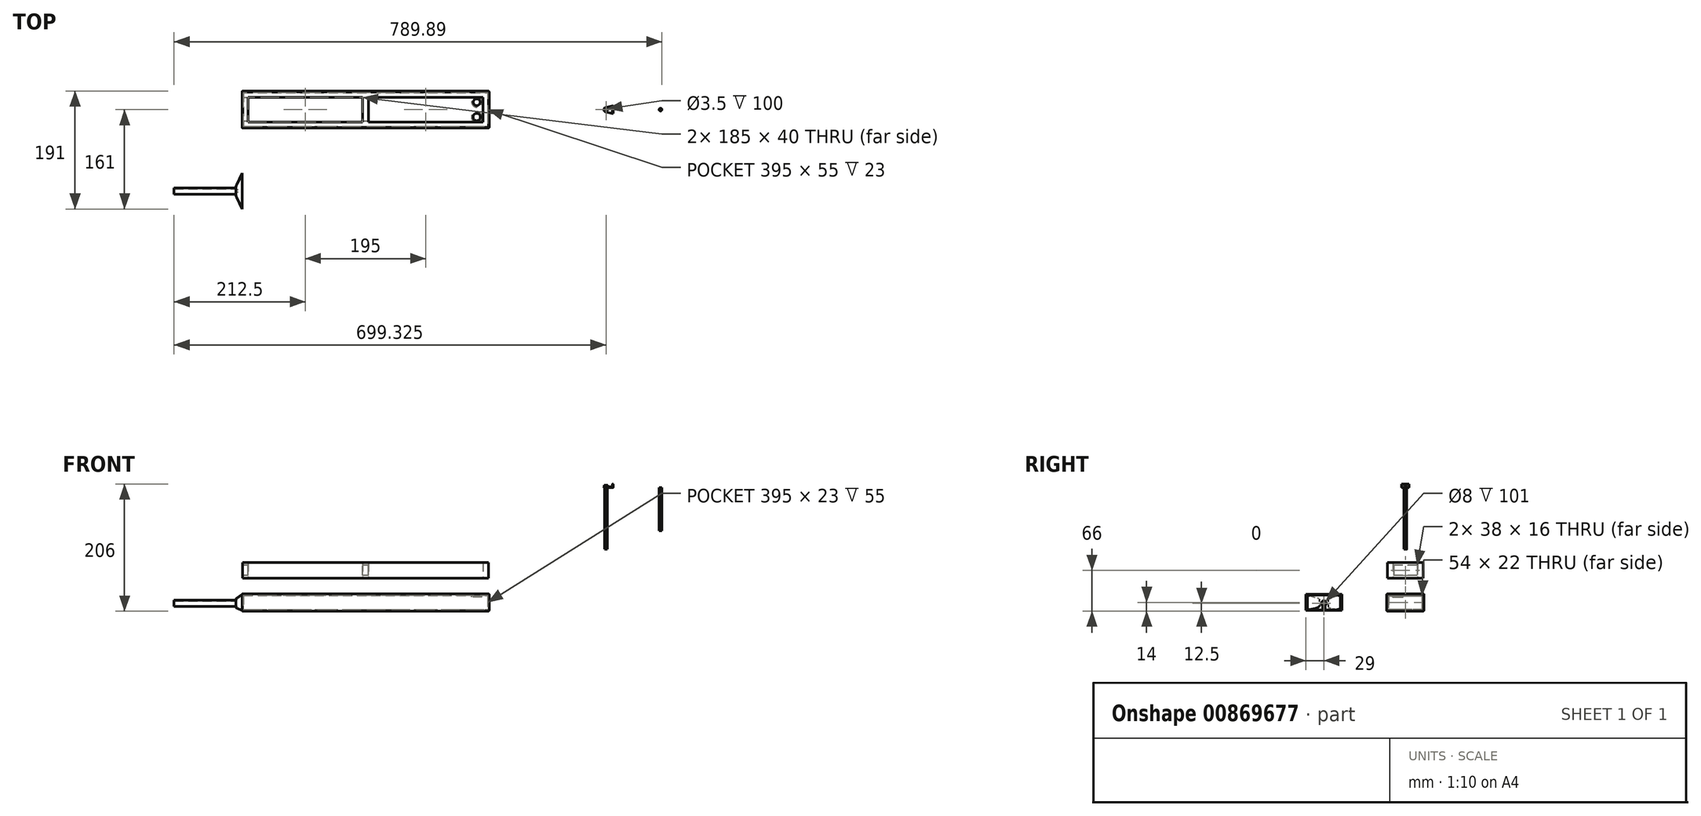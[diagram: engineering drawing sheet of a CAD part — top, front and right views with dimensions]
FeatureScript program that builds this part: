
annotation { "Feature Type Name" : "Feature", "Feature Type Description" : "" }
export const myFeature = defineFeature(function(context is Context, id is Id, definition is map)
    precondition{}
    {
        {
            var Q0;
            Q0=qCreatedBy(makeId("Top.planeOp"),FACE);
            var sketch = newSketch(context, id + "F0", { "sketchPlane" : qUnion([Q0])});
            skLineSegment(sketch, "E0.bottom", {"start": v(-200, 30) * mm, "end": v(200, 30) * mm});
            skLineSegment(sketch, "E0.top", {"start": v(-200, -30) * mm, "end": v(200, -30) * mm});
            skLineSegment(sketch, "E0.left", {"start": v(-200, 30) * mm, "end": v(-200, -30) * mm});
            skLineSegment(sketch, "E0.right", {"start": v(200, 30) * mm, "end": v(200, -30) * mm});
            skPoint(sketch, "E0.middle", {"position": v(0, 0) * mm});
            skSolve(sketch);
        }
        {
            var Q0;
            Q0 = qSketchRegion(id + "F0", true);
            extrude(context, id + "F1", {"entities" : qUnion([Q0]), "depth" : 25 * mm, "offsetDistance" : 25 * mm});
        }
        {
            var Q0;
            Q0=makeQuery(id+"F1.opExtrude","SWEPT_FACE",FACE,{"disambiguationData":[OSD([sQuery(id+"F0.wireOp",EDGE,"E0.right")])]});
            var sketch = newSketch(context, id + "F2", { "sketchPlane" : qUnion([Q0])});
            skLineSegment(sketch, "E1", {"start": v(0, 25) * mm, "end": v(0, 0) * mm, "construction": true});
            skLineSegment(sketch, "E2", {"start": v(-30, 12.5) * mm, "end": v(30, 12.5) * mm, "construction": true});
            skPoint(sketch, "E3", {"position": v(0, 12.5) * mm});
            skCircle(sketch, "E4", {"center": v(0, 12.5) * mm, "radius": 5 * mm});
            skSolve(sketch);
        }
        {
            var Q0;
            Q0=makeQuery(id+"F1.opExtrude","CAP_FACE",FACE,{"disambiguationData":[OSD([sQuery(id+"F0.wireOp",EDGE,"E0.bottom"),sQuery(id+"F0.wireOp",EDGE,"E0.top"),sQuery(id+"F0.wireOp",EDGE,"E0.left"),sQuery(id+"F0.wireOp",EDGE,"E0.right")])],"isStart":false});
            cPlane(context, id + "F3", {"entities" : qUnion([Q0]), "cplaneType" : CPlaneType.OFFSET, "offset" : 3 * mm, "width" : 150 * mm, "height" : 150 * mm});
        }
        {
            var Q0;
            Q0=qCreatedBy(id+"F3.planeOp",FACE);
            var sketch = newSketch(context, id + "F4", { "sketchPlane" : qUnion([Q0])});
            skLineSegment(sketch, "E5", {"start": v(200.7, 0) * mm, "end": v(-212.41, 0) * mm, "construction": true});
            skLineSegment(sketch, "E6.0", {"start": v(200, -30) * mm, "end": v(200, 30) * mm});
            skLineSegment(sketch, "E7.0", {"start": v(-200, 30) * mm, "end": v(-200, -30) * mm});
            skLineSegment(sketch, "E8.0", {"start": v(-200, 30) * mm, "end": v(200, 30) * mm});
            skLineSegment(sketch, "E9.0", {"start": v(-200, -30) * mm, "end": v(200, -30) * mm});
            skLineSegment(sketch, "E10", {"start": v(200, 12) * mm, "end": v(-200, 12) * mm, "construction": true});
            skLineSegment(sketch, "E11", {"start": v(200, -12) * mm, "end": v(-200, -12) * mm, "construction": true});
            skLineSegment(sketch, "E12", {"start": v(180, 30) * mm, "end": v(180, -30) * mm, "construction": true});
            skCircle(sketch, "E13", {"center": v(180, 12) * mm, "radius": 6 * mm});
            skCircle(sketch, "E14.MirrorC", {"center": v(180, -12) * mm, "radius": 6 * mm});
            skCircle(sketch, "E15", {"center": v(180, 12) * mm, "radius": 5.5 * mm});
            skCircle(sketch, "E16", {"center": v(180, -12) * mm, "radius": 5.5 * mm});
            skLineSegment(sketch, "E17", {"start": v(0, 0) * mm, "end": v(0, 30) * mm, "construction": true});
            skLineSegment(sketch, "E18", {"start": v(-100, 30) * mm, "end": v(-100, -30) * mm, "construction": true});
            skLineSegment(sketch, "E19", {"start": v(-50, 30) * mm, "end": v(-50, -30) * mm, "construction": true});
            skLineSegment(sketch, "E20", {"start": v(-150, 30) * mm, "end": v(-150, -30) * mm, "construction": true});
            skLineSegment(sketch, "E21.MirrorCS", {"start": v(50, 30) * mm, "end": v(50, -30) * mm, "construction": true});
            skLineSegment(sketch, "E22.MirrorCS", {"start": v(100, 30) * mm, "end": v(100, -30) * mm, "construction": true});
            skLineSegment(sketch, "E23.MirrorCS", {"start": v(150, 30) * mm, "end": v(150, -30) * mm, "construction": true});
            skPoint(sketch, "E24", {"position": v(-150, 0) * mm});
            skPoint(sketch, "E25", {"position": v(150, 0) * mm});
            skSolve(sketch);
        }
        {
            var Q0;
            Q0 = qSketchRegion(id + "F4", true);
            var Q1;
            Q1=makeQuery(id+"F4.imprint","IMPRINT",FACE,{"disambiguationData":[TD([[makeQuery(id+"F4.imprint","IMPRINT",EDGE,{"derivedFrom":sQuery(id+"F4.wireOp",EDGE,"E14.MirrorC")}),-1.0]])]});
            var Q2;
            Q2=makeQuery(id+"F4.imprint","IMPRINT",FACE,{"disambiguationData":[TD([[makeQuery(id+"F4.imprint","IMPRINT",EDGE,{"derivedFrom":sQuery(id+"F4.wireOp",EDGE,"E13")}),1.0]])]});
            extrude(context, id + "F5", {"entities" : qUnion([Q0, Q1, Q2]), "operationType" : NewBodyOperationType.ADD, "endBound" : BoundingType.UP_TO_NEXT, "oppositeDirection" : true, "depth" : 25 * mm, "offsetDistance" : 25 * mm});
        }
        {
            var Q0;
            Q0=makeQuery(id+"F5.boolean.opBoolean","SPLIT",FACE,{"disambiguationData":[TD([makeQuery(id+"F5.opExtrude","SWEPT_FACE",FACE,{"disambiguationData":[OSD([sQuery(id+"F4.wireOp",EDGE,"E15")])]})])],"derivedFrom":makeQuery(id+"F1.opExtrude","CAP_FACE",FACE,{"disambiguationData":[OSD([sQuery(id+"F0.wireOp",EDGE,"E0.bottom"),sQuery(id+"F0.wireOp",EDGE,"E0.top"),sQuery(id+"F0.wireOp",EDGE,"E0.left"),sQuery(id+"F0.wireOp",EDGE,"E0.right")])],"isStart":false})});
            var Q1;
            Q1=makeQuery(id+"F5.boolean.opBoolean","SPLIT",FACE,{"disambiguationData":[TD([makeQuery(id+"F5.opExtrude","SWEPT_FACE",FACE,{"disambiguationData":[OSD([sQuery(id+"F4.wireOp",EDGE,"E16")])]})])],"derivedFrom":makeQuery(id+"F1.opExtrude","CAP_FACE",FACE,{"disambiguationData":[OSD([sQuery(id+"F0.wireOp",EDGE,"E0.bottom"),sQuery(id+"F0.wireOp",EDGE,"E0.top"),sQuery(id+"F0.wireOp",EDGE,"E0.left"),sQuery(id+"F0.wireOp",EDGE,"E0.right")])],"isStart":false})});
            shell(context, id + "F6", {"entities" : qUnion([Q0, Q1]), "thickness" : 2.5 * mm});
        }
        {
            var Q0;
            Q0=makeQuery(id+"F5.opExtrude","CAP_EDGE",EDGE,{"disambiguationData":[OSD([sQuery(id+"F4.wireOp",EDGE,"E9.0")])],"isStart":true});
            var Q1;
            Q1=makeQuery(id+"F5.opExtrude","CAP_EDGE",EDGE,{"disambiguationData":[OSD([sQuery(id+"F4.wireOp",EDGE,"E8.0")])],"isStart":true});
            var Q2;
            Q2=makeQuery(id+"F1.opExtrude","CAP_EDGE",EDGE,{"disambiguationData":[OSD([sQuery(id+"F0.wireOp",EDGE,"E0.top")])],"isStart":true});
            var Q3;
            Q3=makeQuery(id+"F1.opExtrude","CAP_EDGE",EDGE,{"disambiguationData":[OSD([sQuery(id+"F0.wireOp",EDGE,"E0.bottom")])],"isStart":true});
            var Q4;
            Q4=makeQuery(id+"F1.opExtrude","CAP_EDGE",EDGE,{"disambiguationData":[OSD([sQuery(id+"F0.wireOp",EDGE,"E0.right")])],"isStart":true});
            var Q5;
            Q5=makeQuery(id+"F5.boolean.opBoolean","MERGE",EDGE,{"derivedFrom":[makeQuery(id+"F1.opExtrude","SWEPT_EDGE",EDGE,{"disambiguationData":[OSD([sQuery(id+"F0.wireOp",EDGE,"E0.top"),sQuery(id+"F0.wireOp",EDGE,"E0.right")])]}),makeQuery(id+"F5.opExtrude","SWEPT_EDGE",EDGE,{"disambiguationData":[OSD([sQuery(id+"F4.wireOp",EDGE,"E6.0"),sQuery(id+"F4.wireOp",EDGE,"E9.0")])]})]});
            var Q6;
            Q6=makeQuery(id+"F5.opExtrude","CAP_EDGE",EDGE,{"disambiguationData":[OSD([sQuery(id+"F4.wireOp",EDGE,"E6.0")])],"isStart":true});
            var Q7;
            Q7=makeQuery(id+"F5.boolean.opBoolean","MERGE",EDGE,{"derivedFrom":[makeQuery(id+"F1.opExtrude","SWEPT_EDGE",EDGE,{"disambiguationData":[OSD([sQuery(id+"F0.wireOp",EDGE,"E0.bottom"),sQuery(id+"F0.wireOp",EDGE,"E0.right")])]}),makeQuery(id+"F5.opExtrude","SWEPT_EDGE",EDGE,{"disambiguationData":[OSD([sQuery(id+"F4.wireOp",EDGE,"E6.0"),sQuery(id+"F4.wireOp",EDGE,"E8.0")])]})]});
            var Q8;
            Q8=makeQuery(id+"F1.opExtrude","CAP_EDGE",EDGE,{"disambiguationData":[OSD([sQuery(id+"F0.wireOp",EDGE,"E0.left")])],"isStart":true});
            var Q9;
            {var subQ0=sQuery(id+"F0.wireOp",EDGE,"E0.left");var subQ1=sQuery(id+"F0.wireOp",EDGE,"E0.top");Q9=makeQuery(id+"F5.boolean.opBoolean","MERGE",EDGE,{"derivedFrom":[makeQuery(id+"F1.opExtrude","SWEPT_EDGE",EDGE,{"disambiguationData":[OSD([subQ1,subQ0])]}),makeQuery(id+"F5.opExtrude","SWEPT_EDGE",EDGE,{"disambiguationData":[OSD([subQ1,subQ0])]})]});}
            var Q10;
            Q10=makeQuery(id+"F5.opExtrude","CAP_EDGE",EDGE,{"disambiguationData":[OSD([sQuery(id+"F4.wireOp",EDGE,"E7.0")])],"isStart":true});
            var Q11;
            {var subQ0=sQuery(id+"F0.wireOp",EDGE,"E0.left");var subQ1=sQuery(id+"F0.wireOp",EDGE,"E0.bottom");Q11=makeQuery(id+"F5.boolean.opBoolean","MERGE",EDGE,{"derivedFrom":[makeQuery(id+"F1.opExtrude","SWEPT_EDGE",EDGE,{"disambiguationData":[OSD([subQ1,subQ0])]}),makeQuery(id+"F5.opExtrude","SWEPT_EDGE",EDGE,{"disambiguationData":[OSD([subQ1,subQ0])]})]});}
            fillet(context, id + "F7", {"entities" : qUnion([Q0, Q1, Q2, Q3, Q4, Q5, Q6, Q7, Q8, Q9, Q10, Q11]), "radius" : 1 * mm, "tangentPropagation" : true, "allowEdgeOverflow" : false});
        }
        {
            var Q0;
            Q0=makeQuery(id+"F5.opExtrude","CAP_FACE",FACE,{"disambiguationData":[OSD([sQuery(id+"F4.wireOp",EDGE,"E6.0"),sQuery(id+"F4.wireOp",EDGE,"E7.0"),sQuery(id+"F4.wireOp",EDGE,"E8.0"),sQuery(id+"F4.wireOp",EDGE,"E9.0"),sQuery(id+"F4.wireOp",EDGE,"E15"),sQuery(id+"F4.wireOp",EDGE,"E16")])],"isStart":true});
            cPlane(context, id + "F8", {"entities" : qUnion([Q0]), "cplaneType" : CPlaneType.OFFSET, "offset" : 25 * mm, "width" : 150 * mm, "height" : 150 * mm});
        }
        {
            var Q0;
            Q0=qCreatedBy(id+"F8.planeOp",FACE);
            var sketch = newSketch(context, id + "F9", { "sketchPlane" : qUnion([Q0])});
            skLineSegment(sketch, "E26.bottom", {"start": v(-190, 20) * mm, "end": v(-5, 20) * mm});
            skLineSegment(sketch, "E26.top", {"start": v(-190, -20) * mm, "end": v(-5, -20) * mm});
            skLineSegment(sketch, "E26.left", {"start": v(-190, 20) * mm, "end": v(-190, -20) * mm});
            skLineSegment(sketch, "E26.right", {"start": v(-5, 20) * mm, "end": v(-5, -20) * mm});
            skLineSegment(sketch, "E27", {"start": v(0, 37.6) * mm, "end": v(0, -41.86) * mm, "construction": true});
            skLineSegment(sketch, "E28.1.0.0", {"start": v(5, 20) * mm, "end": v(5, -20) * mm});
            skLineSegment(sketch, "E28.1.0.1", {"start": v(5, 20) * mm, "end": v(190, 20) * mm});
            skLineSegment(sketch, "E28.1.0.2", {"start": v(5, -20) * mm, "end": v(190, -20) * mm});
            skLineSegment(sketch, "E28.1.0.3", {"start": v(190, 20) * mm, "end": v(190, -20) * mm});
            skLineSegment(sketch, "E28.direction1", {"start": v(-190, -20) * mm, "end": v(5, -20) * mm, "construction": true});
            skLineSegment(sketch, "E29.0", {"start": v(-199, 30) * mm, "end": v(199, 30) * mm});
            skLineSegment(sketch, "E30.0", {"start": v(199, -30) * mm, "end": v(-199, -30) * mm});
            skLineSegment(sketch, "E31.0", {"start": v(-200, -29) * mm, "end": v(-200, 29) * mm});
            skLineSegment(sketch, "E32.0", {"start": v(200, -30) * mm, "end": v(200, 30) * mm});
            skLineSegment(sketch, "E33.0", {"start": v(199, 29) * mm, "end": v(-199, 29) * mm});
            skLineSegment(sketch, "E34.0", {"start": v(199, -29) * mm, "end": v(199, 29) * mm});
            skLineSegment(sketch, "E35.0", {"start": v(-199, -29) * mm, "end": v(199, -29) * mm});
            skLineSegment(sketch, "E36.0", {"start": v(-199, 29) * mm, "end": v(-199, -29) * mm});
            skSolve(sketch);
        }
        {
            var Q0;
            Q0 = qSketchRegion(id + "F9", true);
            extrude(context, id + "F10", {"entities" : qUnion([Q0]), "depth" : 26 * mm, "offsetDistance" : 25 * mm});
        }
        {
            var Q0;
            Q0=makeQuery(id+"F5.boolean.opBoolean","MERGE",FACE,{"derivedFrom":[makeQuery(id+"F1.opExtrude","SWEPT_FACE",FACE,{"disambiguationData":[OSD([sQuery(id+"F0.wireOp",EDGE,"E0.left")])]}),makeQuery(id+"F5.opExtrude","SWEPT_FACE",FACE,{"disambiguationData":[OSD([sQuery(id+"F4.wireOp",EDGE,"E7.0")])]})]});
            var sketch = newSketch(context, id + "F11", { "sketchPlane" : qUnion([Q0])});
            skLineSegment(sketch, "E37.bottom", {"start": v(29, 27) * mm, "end": v(-29, 27) * mm});
            skLineSegment(sketch, "E37.top", {"start": v(29, 1) * mm, "end": v(-29, 1) * mm});
            skLineSegment(sketch, "E37.left", {"start": v(29, 27) * mm, "end": v(29, 1) * mm});
            skLineSegment(sketch, "E37.right", {"start": v(-29, 27) * mm, "end": v(-29, 1) * mm});
            skPoint(sketch, "E37.middle", {"position": v(0, 14) * mm});
            skSolve(sketch);
        }
        {
            var Q0;
            Q0=makeQuery(id+"F11.imprint","IMPRINT",FACE,{"disambiguationData":[TD([[makeQuery(id+"F11.imprint","IMPRINT",EDGE,{"derivedFrom":sQuery(id+"F11.wireOp",EDGE,"E37.bottom")}),1.0]])]});
            cPlane(context, id + "F12", {"entities" : qUnion([Q0]), "cplaneType" : CPlaneType.OFFSET, "offset" : 10 * mm, "width" : 150 * mm, "height" : 150 * mm});
        }
        {
            var Q0;
            Q0=qCreatedBy(id+"F12.planeOp",FACE);
            var sketch = newSketch(context, id + "F13", { "sketchPlane" : qUnion([Q0])});
            skLineSegment(sketch, "E38.bottom", {"start": v(7.5, 20) * mm, "end": v(-7.5, 20) * mm});
            skLineSegment(sketch, "E38.top", {"start": v(7.5, 5) * mm, "end": v(-7.5, 5) * mm});
            skLineSegment(sketch, "E38.left", {"start": v(7.5, 20) * mm, "end": v(7.5, 5) * mm});
            skLineSegment(sketch, "E38.right", {"start": v(-7.5, 20) * mm, "end": v(-7.5, 5) * mm});
            skPoint(sketch, "E38.middle", {"position": v(0, 12.5) * mm});
            skSolve(sketch);
        }
        {
            var Q1;
            Q1=makeQuery(id+"F11.imprint","IMPRINT",FACE,{"disambiguationData":[TD([[makeQuery(id+"F11.imprint","IMPRINT",EDGE,{"derivedFrom":sQuery(id+"F11.wireOp",EDGE,"E37.bottom")}),1.0]])]});
            var Q2;
            Q2=makeQuery(id+"F13.imprint","IMPRINT",FACE,{"disambiguationData":[TD([[makeQuery(id+"F13.imprint","IMPRINT",EDGE,{"derivedFrom":sQuery(id+"F13.wireOp",EDGE,"E38.bottom")}),1.0]])]});
            loft(context, id + "F14", {"sheetProfilesArray" : [{ "sheetProfileEntities" : qUnion([Q1]) }, { "sheetProfileEntities" : qUnion([Q2]) }]});
        }
        {
            var Q0;
            Q0=makeQuery(id+"F14.opLoft","SWEPT_BODY",BODY,{"disambiguationData":[OSD([makeQuery(id+"F11.imprint","IMPRINT",FACE,{"disambiguationData":[TD([[makeQuery(id+"F11.imprint","IMPRINT",EDGE,{"derivedFrom":sQuery(id+"F11.wireOp",EDGE,"E37.bottom")}),1.0]])]}),makeQuery(id+"F13.imprint","IMPRINT",FACE,{"disambiguationData":[TD([[makeQuery(id+"F13.imprint","IMPRINT",EDGE,{"derivedFrom":sQuery(id+"F13.wireOp",EDGE,"E38.bottom")}),1.0]])]})])]});
            transform(context, id + "F15", {"entities" : qUnion([Q0]), "transformType" : TransformType.TRANSLATION_3D, "dx" : 0 * mm, "dy" : -132 * mm, "dz" : 0 * mm, "makeCopy" : false});
        }
        {
            var Q0;
            Q0=makeQuery(id+"F5.boolean.opBoolean","MERGE",FACE,{"derivedFrom":[makeQuery(id+"F1.opExtrude","SWEPT_FACE",FACE,{"disambiguationData":[OSD([sQuery(id+"F0.wireOp",EDGE,"E0.left")])]}),makeQuery(id+"F5.opExtrude","SWEPT_FACE",FACE,{"disambiguationData":[OSD([sQuery(id+"F4.wireOp",EDGE,"E7.0")])]})]});
            var sketch = newSketch(context, id + "F16", { "sketchPlane" : qUnion([Q0])});
            skLineSegment(sketch, "E39.bottom", {"start": v(27, 25) * mm, "end": v(-27, 25) * mm});
            skLineSegment(sketch, "E39.top", {"start": v(27, 3) * mm, "end": v(-27, 3) * mm});
            skLineSegment(sketch, "E39.left", {"start": v(27, 25) * mm, "end": v(27, 3) * mm});
            skLineSegment(sketch, "E39.right", {"start": v(-27, 25) * mm, "end": v(-27, 3) * mm});
            skPoint(sketch, "E39.middle", {"position": v(0, 12.5) * mm});
            skSolve(sketch);
        }
        {
            var Q0;
            Q0 = qSketchRegion(id + "F16", true);
            extrude(context, id + "F17", {"entities" : qUnion([Q0]), "operationType" : NewBodyOperationType.REMOVE, "oppositeDirection" : true, "depth" : 5 * mm, "offsetDistance" : 25 * mm});
        }
        {
            var Q0;
            Q0=makeQuery(id+"F14.opLoft","CAP_FACE",FACE,{"disambiguationData":[OSD([makeQuery(id+"F13.imprint","IMPRINT",FACE,{"disambiguationData":[TD([[makeQuery(id+"F13.imprint","IMPRINT",EDGE,{"derivedFrom":sQuery(id+"F13.wireOp",EDGE,"E38.bottom")}),1.0]])]})])],"isStart":true});
            var sketch = newSketch(context, id + "F18", { "sketchPlane" : qUnion([Q0])});
            skLineSegment(sketch, "E40", {"start": v(124.5, 20) * mm, "end": v(139.5, 5) * mm, "construction": true});
            skLineSegment(sketch, "E41", {"start": v(139.5, 20) * mm, "end": v(124.5, 5) * mm, "construction": true});
            skPoint(sketch, "E42", {"position": v(132, 12.5) * mm});
            skCircle(sketch, "E43", {"center": v(132, 12.5) * mm, "radius": 5 * mm});
            skSolve(sketch);
        }
        {
            var Q0;
            Q0 = qSketchRegion(id + "F18", true);
            extrude(context, id + "F19", {"entities" : qUnion([Q0]), "operationType" : NewBodyOperationType.ADD, "depth" : 100 * mm, "offsetDistance" : 25 * mm});
        }
        {
            var Q0;
            Q0=makeQuery(id+"F19.opExtrude","CAP_FACE",FACE,{"disambiguationData":[OSD([sQuery(id+"F18.wireOp",EDGE,"E43")])],"isStart":false});
            var Q1;
            Q1=makeQuery(id+"F14.opLoft","CAP_FACE",FACE,{"disambiguationData":[OSD([makeQuery(id+"F11.imprint","IMPRINT",FACE,{"disambiguationData":[TD([[makeQuery(id+"F11.imprint","IMPRINT",EDGE,{"derivedFrom":sQuery(id+"F11.wireOp",EDGE,"E37.bottom")}),1.0]])]})])],"isStart":true});
            shell(context, id + "F20", {"entities" : qUnion([Q0, Q1]), "thickness" : 1 * mm});
        }
        {
            var Q0;
            Q0=makeQuery(id+"F14.opLoft","MID_CAP_EDGE",EDGE,{"disambiguationData":[OSD([sQuery(id+"F13.wireOp",EDGE,"E38.bottom"),sQuery(id+"F13.wireOp",EDGE,"E38.top"),sQuery(id+"F13.wireOp",EDGE,"E38.left")])],"capPos":1.0});
            var Q1;
            Q1=makeQuery(id+"F14.opLoft","MID_CAP_EDGE",EDGE,{"disambiguationData":[OSD([sQuery(id+"F13.wireOp",EDGE,"E38.bottom"),sQuery(id+"F13.wireOp",EDGE,"E38.left"),sQuery(id+"F13.wireOp",EDGE,"E38.right")])],"capPos":1.0});
            var Q2;
            Q2=makeQuery(id+"F14.opLoft","MID_CAP_EDGE",EDGE,{"disambiguationData":[OSD([sQuery(id+"F13.wireOp",EDGE,"E38.bottom"),sQuery(id+"F13.wireOp",EDGE,"E38.top"),sQuery(id+"F13.wireOp",EDGE,"E38.right")])],"capPos":1.0});
            var Q3;
            Q3=makeQuery(id+"F14.opLoft","MID_CAP_EDGE",EDGE,{"disambiguationData":[OSD([sQuery(id+"F13.wireOp",EDGE,"E38.top"),sQuery(id+"F13.wireOp",EDGE,"E38.left"),sQuery(id+"F13.wireOp",EDGE,"E38.right")])],"capPos":1.0});
            fillet(context, id + "F21", {"entities" : qUnion([Q0, Q1, Q2, Q3]), "radius" : 3 * mm, "tangentPropagation" : true, "allowEdgeOverflow" : false});
        }
        {
            var Q0;
            Q0=makeQuery(id+"F20.opShell","OFFSET_EDGE",EDGE,{"disambiguationData":[OSD([sQuery(id+"F13.wireOp",EDGE,"E38.bottom"),sQuery(id+"F13.wireOp",EDGE,"E38.top"),sQuery(id+"F13.wireOp",EDGE,"E38.left")])]});
            var Q1;
            Q1=makeQuery(id+"F20.opShell","OFFSET_EDGE",EDGE,{"disambiguationData":[OSD([sQuery(id+"F13.wireOp",EDGE,"E38.bottom"),sQuery(id+"F13.wireOp",EDGE,"E38.top"),sQuery(id+"F13.wireOp",EDGE,"E38.right")])]});
            var Q2;
            Q2=makeQuery(id+"F20.opShell","OFFSET_EDGE",EDGE,{"disambiguationData":[OSD([sQuery(id+"F13.wireOp",EDGE,"E38.bottom"),sQuery(id+"F13.wireOp",EDGE,"E38.left"),sQuery(id+"F13.wireOp",EDGE,"E38.right")])]});
            var Q3;
            Q3=makeQuery(id+"F20.opShell","OFFSET_EDGE",EDGE,{"disambiguationData":[OSD([sQuery(id+"F13.wireOp",EDGE,"E38.top"),sQuery(id+"F13.wireOp",EDGE,"E38.left"),sQuery(id+"F13.wireOp",EDGE,"E38.right")])]});
            var Q4;
            Q4=makeQuery(id+"F20.opShell","OFFSET_EDGE",EDGE,{"disambiguationData":[OSD([sQuery(id+"F11.wireOp",EDGE,"E37.bottom"),sQuery(id+"F11.wireOp",EDGE,"E37.right"),sQuery(id+"F13.wireOp",EDGE,"E38.bottom"),sQuery(id+"F13.wireOp",EDGE,"E38.right")])]});
            var Q5;
            Q5=makeQuery(id+"F20.opShell","OFFSET_EDGE",EDGE,{"disambiguationData":[OSD([sQuery(id+"F11.wireOp",EDGE,"E37.top"),sQuery(id+"F11.wireOp",EDGE,"E37.right"),sQuery(id+"F13.wireOp",EDGE,"E38.top"),sQuery(id+"F13.wireOp",EDGE,"E38.right")])]});
            var Q6;
            Q6=makeQuery(id+"F20.opShell","OFFSET_EDGE",EDGE,{"disambiguationData":[OSD([sQuery(id+"F11.wireOp",EDGE,"E37.bottom"),sQuery(id+"F11.wireOp",EDGE,"E37.left"),sQuery(id+"F13.wireOp",EDGE,"E38.bottom"),sQuery(id+"F13.wireOp",EDGE,"E38.left")])]});
            fillet(context, id + "F22", {"entities" : qUnion([Q0, Q1, Q2, Q3, Q4, Q5, Q6]), "radius" : 5 * mm, "tangentPropagation" : true, "allowEdgeOverflow" : false});
        }
        {
            var Q0;
            Q0=makeQuery(id+"F10.opExtrude","SWEPT_FACE",FACE,{"disambiguationData":[OSD([sQuery(id+"F9.wireOp",EDGE,"E36.0")])]});
            var sketch = newSketch(context, id + "F23", { "sketchPlane" : qUnion([Q0])});
            skLineSegment(sketch, "E44.bottom", {"start": v(-19, 74) * mm, "end": v(19, 74) * mm});
            skLineSegment(sketch, "E44.top", {"start": v(-19, 58) * mm, "end": v(19, 58) * mm});
            skLineSegment(sketch, "E44.left", {"start": v(-19, 74) * mm, "end": v(-19, 58) * mm});
            skLineSegment(sketch, "E44.right", {"start": v(19, 74) * mm, "end": v(19, 58) * mm});
            skSolve(sketch);
        }
        {
            var Q0;
            Q0 = qSketchRegion(id + "F23", true);
            extrude(context, id + "F24", {"entities" : qUnion([Q0]), "operationType" : NewBodyOperationType.REMOVE, "oppositeDirection" : true, "depth" : 260 * mm, "offsetDistance" : 25 * mm});
        }
        {
            var Q0;
            Q0=qCreatedBy(makeId("Right.planeOp"),FACE);
            cPlane(context, id + "F25", {"entities" : qUnion([Q0]), "cplaneType" : CPlaneType.OFFSET, "offset" : 400 * mm, "width" : 150 * mm, "height" : 150 * mm});
        }
        {
            var Q0;
            Q0=qCreatedBy(id+"F25.planeOp",FACE);
            var sketch = newSketch(context, id + "F26", { "sketchPlane" : qUnion([Q0])});
            skLineSegment(sketch, "E45", {"start": v(0, 0) * mm, "end": v(0, 200) * mm, "construction": true});
            skSolve(sketch);
        }
        {
            var Q0;
            Q0=qCreatedBy(makeId("Top.planeOp"),FACE);
            var Q1;
            Q1=sQuery(id+"F26.wireOp",VERTEX,"E45.end");
            cPlane(context, id + "F27", {"entities" : qUnion([Q0, Q1]), "cplaneType" : CPlaneType.PLANE_POINT, "offset" : 25 * mm, "width" : 150 * mm, "height" : 150 * mm});
        }
        {
            var Q0;
            Q0=qCreatedBy(id+"F27.planeOp",FACE);
            var sketch = newSketch(context, id + "F28", { "sketchPlane" : qUnion([Q0])});
            skLineSegment(sketch, "E46.bottom", {"start": v(401, 6) * mm, "end": v(399, 6) * mm});
            skLineSegment(sketch, "E46.top", {"start": v(401, -6) * mm, "end": v(399, -6) * mm});
            skLineSegment(sketch, "E46.left", {"start": v(401, 6) * mm, "end": v(401, -6) * mm});
            skLineSegment(sketch, "E46.right", {"start": v(399, 6) * mm, "end": v(399, -6) * mm});
            skPoint(sketch, "E46.middle", {"position": v(400, 0) * mm});
            skLineSegment(sketch, "E47", {"start": v(313.11, 0) * mm, "end": v(499.34, 0) * mm, "construction": true});
            skLineSegment(sketch, "E48", {"start": v(389.32, -13.78) * mm, "end": v(389.32, -0.28) * mm, "construction": true});
            skArc(sketch, "E49", {"start": v(387.07, 0) * mm, "mid": v(389.32, -2.25) * mm, "end": v(391.57, 0) * mm});
            skLineSegment(sketch, "E50", {"start": v(387, -13.8) * mm, "end": v(387, 0) * mm, "construction": true});
            skLineSegment(sketch, "E51", {"start": v(388.56, -3.53) * mm, "end": v(399, -6) * mm});
            skArc(sketch, "E52.trimOffspring", {"start": v(386, 0) * mm, "mid": v(386.62, -2.24) * mm, "end": v(388.56, -3.53) * mm});
            skLineSegment(sketch, "E53", {"start": v(386, 0) * mm, "end": v(386, -14.1) * mm, "construction": true});
            skArc(sketch, "E54.MirrorCS", {"start": v(386, 0) * mm, "mid": v(386.62, 2.24) * mm, "end": v(388.56, 3.53) * mm});
            skArc(sketch, "E55.MirrorCS", {"start": v(387.07, 0) * mm, "mid": v(389.32, 2.25) * mm, "end": v(391.57, 0) * mm});
            skLineSegment(sketch, "E56.MirrorCS", {"start": v(388.56, 3.53) * mm, "end": v(399, 6) * mm});
            skPoint(sketch, "E57.orphan", {"position": v(387, -3.16) * mm});
            skPoint(sketch, "E58.orphan", {"position": v(387, 3.16) * mm});
            skPoint(sketch, "E59.orphan", {"position": v(389.32, -3.62) * mm});
            skPoint(sketch, "E60.orphan", {"position": v(389.32, 3.62) * mm});
            skSolve(sketch);
        }
        {
            var Q0;
            Q0 = qSketchRegion(id + "F28", true);
            extrude(context, id + "F29", {"entities" : qUnion([Q0]), "depth" : 1 * mm, "offsetDistance" : 25 * mm});
        }
        {
            var Q0;
            Q0=makeQuery(id+"F29.opExtrude","SWEPT_FACE",FACE,{"disambiguationData":[OSD([sQuery(id+"F28.wireOp",EDGE,"E46.left")])]});
            var sketch = newSketch(context, id + "F30", { "sketchPlane" : qUnion([Q0])});
            skLineSegment(sketch, "E61.bottom", {"start": v(-6, 201) * mm, "end": v(6, 201) * mm});
            skLineSegment(sketch, "E61.top", {"start": v(-6, 206) * mm, "end": v(6, 206) * mm});
            skLineSegment(sketch, "E61.left", {"start": v(-6, 201) * mm, "end": v(-6, 206) * mm});
            skLineSegment(sketch, "E61.right", {"start": v(6, 201) * mm, "end": v(6, 206) * mm});
            skSolve(sketch);
        }
        {
            var Q0;
            Q0 = qSketchRegion(id + "F30", true);
            extrude(context, id + "F31", {"entities" : qUnion([Q0]), "operationType" : NewBodyOperationType.ADD, "oppositeDirection" : true, "depth" : 1 * mm, "offsetDistance" : 25 * mm});
        }
        {
            var Q0;
            Q0=makeQuery(id+"F31.opExtrude","CAP_FACE",FACE,{"disambiguationData":[OSD([sQuery(id+"F30.wireOp",EDGE,"E61.bottom"),sQuery(id+"F30.wireOp",EDGE,"E61.top"),sQuery(id+"F30.wireOp",EDGE,"E61.left"),sQuery(id+"F30.wireOp",EDGE,"E61.right")])],"isStart":false});
            var sketch = newSketch(context, id + "F32", { "sketchPlane" : qUnion([Q0])});
            skLineSegment(sketch, "E62", {"start": v(0, 201) * mm, "end": v(0, 206) * mm, "construction": true});
            skLineSegment(sketch, "E63", {"start": v(3, 206) * mm, "end": v(3, 201) * mm, "construction": true});
            skLineSegment(sketch, "E64", {"start": v(-3, 206) * mm, "end": v(-3, 201) * mm, "construction": true});
            skLineSegment(sketch, "E65", {"start": v(6, 203.5) * mm, "end": v(-6, 203.5) * mm, "construction": true});
            skPoint(sketch, "E66", {"position": v(3, 203.5) * mm});
            skPoint(sketch, "E67", {"position": v(-3, 203.5) * mm});
            skPoint(sketch, "E68", {"position": v(0, 203.5) * mm});
            skSolve(sketch);
        }
        {
            var Q0;
            Q0=sQuery(id+"F32.wireOp",VERTEX,"E68");
            var Q1;
            Q1=makeQuery(id+"F29.opExtrude","SWEPT_BODY",BODY,{"disambiguationData":[OSD([sQuery(id+"F28.wireOp",EDGE,"E46.bottom"),sQuery(id+"F28.wireOp",EDGE,"E46.top"),sQuery(id+"F28.wireOp",EDGE,"E46.left"),sQuery(id+"F28.wireOp",EDGE,"E49"),sQuery(id+"F28.wireOp",EDGE,"E51"),sQuery(id+"F28.wireOp",EDGE,"E52.trimOffspring"),sQuery(id+"F28.wireOp",EDGE,"E54.MirrorCS"),sQuery(id+"F28.wireOp",EDGE,"E55.MirrorCS"),sQuery(id+"F28.wireOp",EDGE,"E56.MirrorCS")])]});
            hole(context, id + "F33", {"style" : HoleStyle.SIMPLE, "endStyle" : HoleEndStyle.THROUGH, "holeDiameter" : 2 * mm, "majorDiameter" : 5 * mm, "isTappedThrough" : true, "tappedDepth" : 12 * mm, "tapClearance" : 3, "locations" : qUnion([Q0]), "scope" : qUnion([Q1])});
        }
        {
            var Q0;
            Q0=makeQuery(id+"F29.opExtrude","CAP_EDGE",EDGE,{"disambiguationData":[OSD([sQuery(id+"F28.wireOp",EDGE,"E51")])],"isStart":false});
            var Q1;
            Q1=makeQuery(id+"F29.opExtrude","CAP_EDGE",EDGE,{"disambiguationData":[OSD([sQuery(id+"F28.wireOp",EDGE,"E56.MirrorCS")])],"isStart":false});
            var Q2;
            Q2=makeQuery(id+"F29.opExtrude","CAP_EDGE",EDGE,{"disambiguationData":[OSD([sQuery(id+"F28.wireOp",EDGE,"E56.MirrorCS")])],"isStart":true});
            var Q3;
            Q3=makeQuery(id+"F29.opExtrude","CAP_EDGE",EDGE,{"disambiguationData":[OSD([sQuery(id+"F28.wireOp",EDGE,"E52.trimOffspring")])],"isStart":true});
            var Q4;
            Q4=makeQuery(id+"F29.opExtrude","CAP_EDGE",EDGE,{"disambiguationData":[OSD([sQuery(id+"F28.wireOp",EDGE,"E46.top")])],"isStart":true});
            var Q5;
            Q5=makeQuery(id+"F29.opExtrude","CAP_EDGE",EDGE,{"disambiguationData":[OSD([sQuery(id+"F28.wireOp",EDGE,"E46.bottom")])],"isStart":true});
            var Q6;
            Q6=makeQuery(id+"F29.opExtrude","CAP_EDGE",EDGE,{"disambiguationData":[OSD([sQuery(id+"F28.wireOp",EDGE,"E46.bottom")])],"isStart":false});
            var Q7;
            Q7=makeQuery(id+"F29.opExtrude","CAP_EDGE",EDGE,{"disambiguationData":[OSD([sQuery(id+"F28.wireOp",EDGE,"E46.top")])],"isStart":false});
            var Q8;
            Q8=makeQuery(id+"F31.opExtrude","CAP_EDGE",EDGE,{"disambiguationData":[OSD([sQuery(id+"F30.wireOp",EDGE,"E61.left")])],"isStart":false});
            var Q9;
            Q9=makeQuery(id+"F31.opExtrude","CAP_EDGE",EDGE,{"disambiguationData":[OSD([sQuery(id+"F30.wireOp",EDGE,"E61.right")])],"isStart":false});
            var Q10;
            Q10=makeQuery(id+"F31.opExtrude","CAP_EDGE",EDGE,{"disambiguationData":[OSD([sQuery(id+"F30.wireOp",EDGE,"E61.top")])],"isStart":false});
            var Q11;
            Q11=makeQuery(id+"F31.opExtrude","CAP_EDGE",EDGE,{"disambiguationData":[OSD([sQuery(id+"F30.wireOp",EDGE,"E61.bottom")])],"isStart":false});
            fillet(context, id + "F34", {"entities" : qUnion([Q0, Q1, Q2, Q3, Q4, Q5, Q6, Q7, Q8, Q9, Q10, Q11]), "radius" : 0.3 * mm, "tangentPropagation" : true, "allowEdgeOverflow" : false});
        }
        {
            var Q0;
            Q0=qCreatedBy(id+"F27.planeOp",FACE);
            cPlane(context, id + "F35", {"entities" : qUnion([Q0]), "cplaneType" : CPlaneType.OFFSET, "offset" : 70 * mm, "oppositeDirection" : true, "width" : 150 * mm, "height" : 150 * mm});
        }
        {
            var Q0;
            Q0=makeQuery(id+"F28.imprint","IMPRINT",FACE,{"disambiguationData":[TD([[makeQuery(id+"F28.imprint","IMPRINT",EDGE,{"derivedFrom":sQuery(id+"F28.wireOp",EDGE,"E46.right")}),-1.0]])]});
            var sketch = newSketch(context, id + "F36", { "sketchPlane" : qUnion([Q0])});
            skCircle(sketch, "E69", {"center": v(477.64, 0) * mm, "radius": 2.25 * mm});
            skSolve(sketch);
        }
        {
            var Q0;
            Q0 = qSketchRegion(id + "F36", true);
            extrude(context, id + "F37", {"entities" : qUnion([Q0]), "oppositeDirection" : true, "depth" : 70 * mm, "offsetDistance" : 25 * mm});
        }
        {
            var Q0;
            Q0=makeQuery(id+"F1.opExtrude","CAP_FACE",FACE,{"disambiguationData":[OSD([sQuery(id+"F0.wireOp",EDGE,"E0.bottom"),sQuery(id+"F0.wireOp",EDGE,"E0.top"),sQuery(id+"F0.wireOp",EDGE,"E0.left"),sQuery(id+"F0.wireOp",EDGE,"E0.right")])],"isStart":true});
            var sketch = newSketch(context, id + "F38", { "sketchPlane" : qUnion([Q0])});
            skCircle(sketch, "E70", {"center": v(-150, 0) * mm, "radius": 5 * mm});
            skCircle(sketch, "E71", {"center": v(150, 0) * mm, "radius": 5 * mm});
            skSolve(sketch);
        }
        {
            var Q0;
            Q0 = qSketchRegion(id + "F38", true);
            extrude(context, id + "F39", {"entities" : qUnion([Q0]), "operationType" : NewBodyOperationType.ADD, "endBound" : BoundingType.UP_TO_NEXT, "oppositeDirection" : true, "depth" : 25 * mm, "offsetDistance" : 25 * mm});
        }
        {
            var Q0;
            Q0=makeQuery(id+"F28.imprint","IMPRINT",FACE,{"disambiguationData":[TD([[makeQuery(id+"F28.imprint","IMPRINT",EDGE,{"derivedFrom":sQuery(id+"F28.wireOp",EDGE,"E49")}),1.0]])]});
            var Q1;
            Q1=sQuery(id+"F28.wireOp",EDGE,"E55.MirrorCS");
            var Q2;
            Q2=sQuery(id+"F28.wireOp",EDGE,"E49");
            extrude(context, id + "F40", {"entities" : qUnion([Q0]), "surfaceEntities" : qUnion([Q1, Q2]), "oppositeDirection" : true, "depth" : 100 * mm, "offsetDistance" : 25 * mm});
        }
        {
            var Q0;
            Q0=makeQuery(id+"F40.opExtrude","CAP_FACE",FACE,{"disambiguationData":[OSD([sQuery(id+"F28.wireOp",EDGE,"E49"),sQuery(id+"F28.wireOp",EDGE,"E55.MirrorCS")])],"isStart":false});
            var sketch = newSketch(context, id + "F41", { "sketchPlane" : qUnion([Q0])});
            skCircle(sketch, "E72", {"center": v(389.32, 0) * mm, "radius": 1.75 * mm});
            skSolve(sketch);
        }
        {
            var Q0;
            Q0 = qSketchRegion(id + "F41", true);
            extrude(context, id + "F42", {"entities" : qUnion([Q0]), "operationType" : NewBodyOperationType.REMOVE, "endBound" : BoundingType.THROUGH_ALL, "oppositeDirection" : true, "depth" : 25 * mm, "offsetDistance" : 25 * mm});
        }
        {
            var Q0;
            Q0=makeQuery(id+"F29.opExtrude","CAP_FACE",FACE,{"disambiguationData":[OSD([sQuery(id+"F28.wireOp",EDGE,"E46.bottom"),sQuery(id+"F28.wireOp",EDGE,"E46.top"),sQuery(id+"F28.wireOp",EDGE,"E46.left"),sQuery(id+"F28.wireOp",EDGE,"E49"),sQuery(id+"F28.wireOp",EDGE,"E51"),sQuery(id+"F28.wireOp",EDGE,"E52.trimOffspring"),sQuery(id+"F28.wireOp",EDGE,"E54.MirrorCS"),sQuery(id+"F28.wireOp",EDGE,"E55.MirrorCS"),sQuery(id+"F28.wireOp",EDGE,"E56.MirrorCS")])],"isStart":false});
            var sketch = newSketch(context, id + "F43", { "sketchPlane" : qUnion([Q0])});
            skCircle(sketch, "E73", {"center": v(389.32, 0) * mm, "radius": 2.75 * mm});
            skSolve(sketch);
        }
        {
            var Q0;
            Q0 = qSketchRegion(id + "F43", true);
            extrude(context, id + "F44", {"entities" : qUnion([Q0]), "depth" : 2.5 * mm, "offsetDistance" : 25 * mm, "hasSecondDirection" : true, "secondDirectionOppositeDirection" : true, "secondDirectionDepth" : 1 * mm});
        }
        {
            var Q0;
            Q0=makeQuery(id+"F44.opExtrude","CAP_EDGE",EDGE,{"disambiguationData":[OSD([sQuery(id+"F43.wireOp",EDGE,"E73")])],"isStart":false});
            fillet(context, id + "F45", {"entities" : qUnion([Q0]), "radius" : 0.2 * mm, "tangentPropagation" : true, "allowEdgeOverflow" : false});
        }
        {
            var Q0;
            Q0=makeQuery(id+"F1.opExtrude","CAP_FACE",FACE,{"disambiguationData":[OSD([sQuery(id+"F0.wireOp",EDGE,"E0.bottom"),sQuery(id+"F0.wireOp",EDGE,"E0.top"),sQuery(id+"F0.wireOp",EDGE,"E0.left"),sQuery(id+"F0.wireOp",EDGE,"E0.right")])],"isStart":true});
            var sketch = newSketch(context, id + "F46", { "sketchPlane" : qUnion([Q0])});
            skPoint(sketch, "E74.0", {"position": v(150, 0) * mm});
            skPoint(sketch, "E75.0", {"position": v(-150, 0) * mm});
            skCircle(sketch, "E76", {"center": v(150, 0) * mm, "radius": 5 * mm});
            skCircle(sketch, "E77", {"center": v(-150, 0) * mm, "radius": 5 * mm});
            skSolve(sketch);
        }
        {
            var Q0;
            Q0 = qSketchRegion(id + "F46", true);
            extrude(context, id + "F47", {"entities" : qUnion([Q0]), "operationType" : NewBodyOperationType.ADD, "oppositeDirection" : true, "depth" : 0.1 * mm, "offsetDistance" : 25 * mm});
        }
    });
